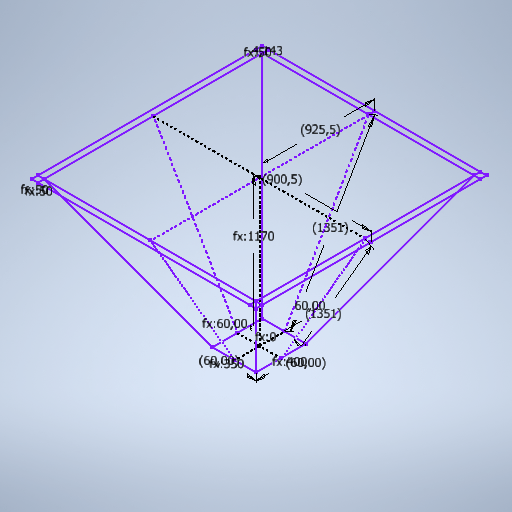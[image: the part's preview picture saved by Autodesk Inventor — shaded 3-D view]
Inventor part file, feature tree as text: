
AUTODESK INVENTOR PART (.ipt)
format: ipt  version: 2025 (Build 290162010, 162A)  size: 304,640 bytes
history: native  units: in
note: dims shown in document units (in); Inventor stores cm internally (conversion verified against a paired STEP export)
features: sketch x2
ambient origin geometry x8: Origin, YZ Plane, XZ Plane, XY Plane, X Axis, Y Axis, Z Axis, Center Point
feature tree (2):
  sketch  "Sketch3"  dims[d16=0.0in d17=15.748in d18=13.7795in d22=0.4188in d23=0.4124in d36=1.9685in d37=1.9685in d38=1.9685in d39=36.437in d41=35.4527in d42=0.1631in d43=53.189in d44=53.189in d46=46.063in d47=60.0deg d48=60.0deg d49=60.0deg d50=60.0deg]
  sketch  "3D Sketch3"
